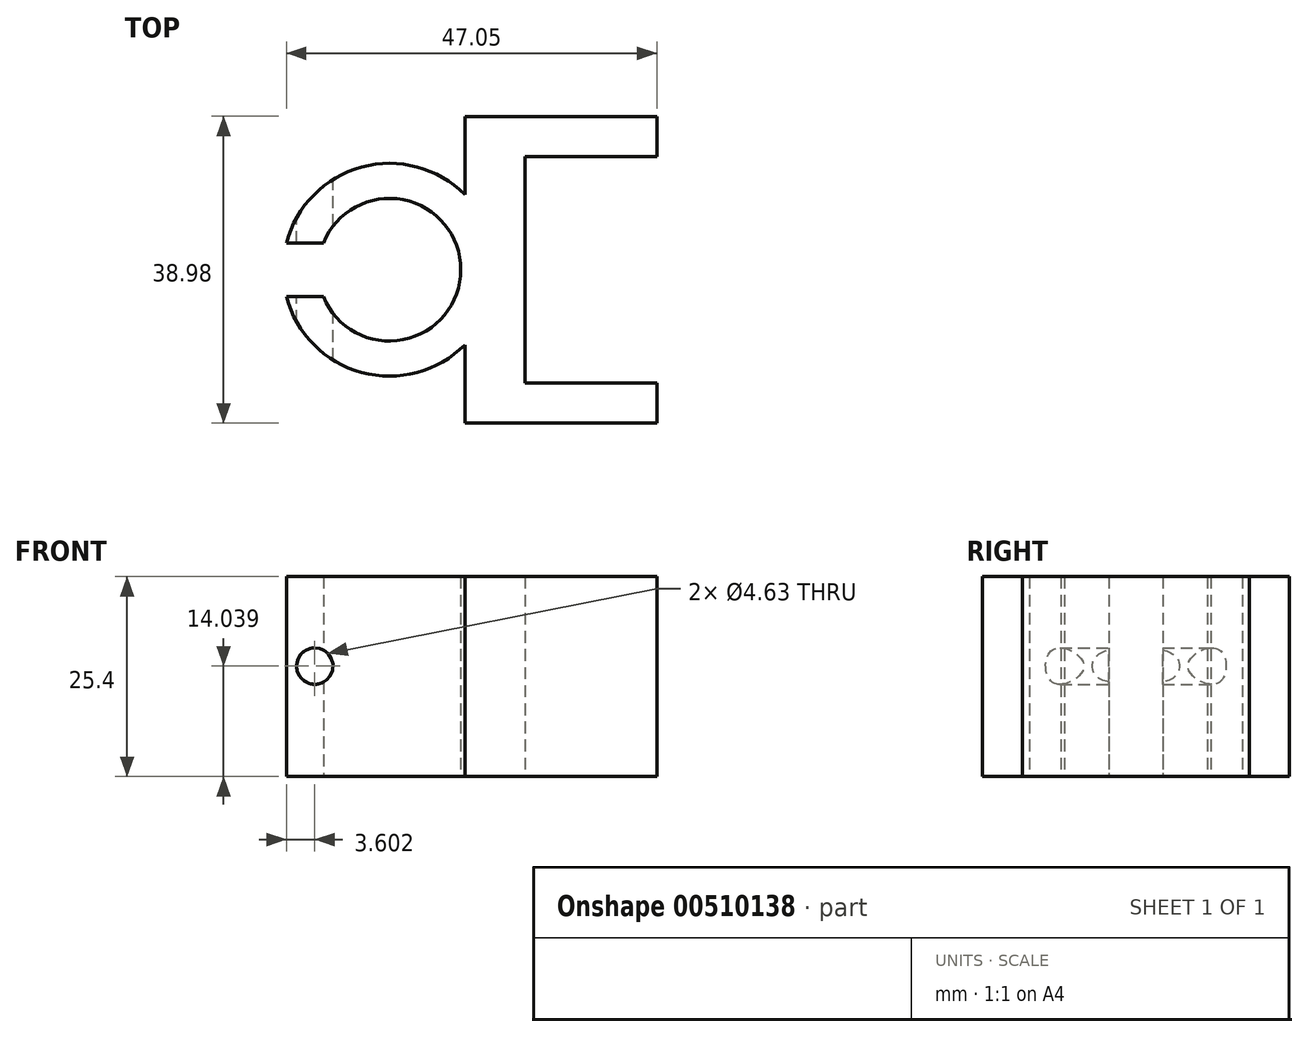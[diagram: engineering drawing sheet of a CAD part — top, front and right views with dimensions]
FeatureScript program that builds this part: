
annotation { "Feature Type Name" : "Feature", "Feature Type Description" : "" }
export const myFeature = defineFeature(function(context is Context, id is Id, definition is map)
    precondition{}
    {
        {
            var Q0;
            Q0=qCreatedBy(makeId("Top.planeOp"),FACE);
            var sketch = newSketch(context, id + "F0", { "sketchPlane" : qUnion([Q0])});
            skCircle(sketch, "E0", {"center": v(-28.96, 0) * mm, "radius": 9.06 * mm});
            skCircle(sketch, "E1", {"center": v(-28.96, 0) * mm, "radius": 13.52 * mm});
            skLineSegment(sketch, "E2.bottom", {"start": v(-19.38, -19.49) * mm, "end": v(-11.76, -19.49) * mm});
            skLineSegment(sketch, "E2.top", {"start": v(-19.38, 19.49) * mm, "end": v(-11.76, 19.49) * mm});
            skLineSegment(sketch, "E2.left", {"start": v(-19.38, -19.49) * mm, "end": v(-19.38, 19.49) * mm});
            skLineSegment(sketch, "E2.right", {"start": v(-11.76, -19.49) * mm, "end": v(-11.76, 19.49) * mm});
            skLineSegment(sketch, "E3.bottom", {"start": v(-11.76, 19.49) * mm, "end": v(5, 19.49) * mm});
            skLineSegment(sketch, "E3.top", {"start": v(-11.76, 14.4) * mm, "end": v(5, 14.4) * mm});
            skLineSegment(sketch, "E3.left", {"start": v(-11.76, 19.49) * mm, "end": v(-11.76, 14.4) * mm});
            skLineSegment(sketch, "E3.right", {"start": v(5, 19.49) * mm, "end": v(5, 14.4) * mm});
            skLineSegment(sketch, "E4.bottom", {"start": v(-11.76, -19.49) * mm, "end": v(5, -19.49) * mm});
            skLineSegment(sketch, "E4.top", {"start": v(-11.76, -14.4) * mm, "end": v(5, -14.4) * mm});
            skLineSegment(sketch, "E4.left", {"start": v(-11.76, -19.49) * mm, "end": v(-11.76, -14.4) * mm});
            skLineSegment(sketch, "E4.right", {"start": v(5, -19.49) * mm, "end": v(5, -14.4) * mm});
            skPoint(sketch, "E5.0", {"position": v(0, 0) * mm});
            skSolve(sketch);
        }
        {
            var Q0;
            Q0 = qSketchRegion(id + "F0", true);
            extrude(context, id + "F1", {"entities" : qUnion([Q0]), "depth" : 25.4 * mm});
        }
        {
            var Q0;
            Q0=makeQuery(id+"F1.opExtrude","CAP_FACE",FACE,{"disambiguationData":[OSD([sQuery(id+"F0.wireOp",EDGE,"E0"),sQuery(id+"F0.wireOp",EDGE,"E1"),sQuery(id+"F0.wireOp",EDGE,"E2.bottom"),sQuery(id+"F0.wireOp",EDGE,"E2.top"),sQuery(id+"F0.wireOp",EDGE,"E2.left"),sQuery(id+"F0.wireOp",EDGE,"E2.right"),sQuery(id+"F0.wireOp",EDGE,"E3.bottom"),sQuery(id+"F0.wireOp",EDGE,"E3.top"),sQuery(id+"F0.wireOp",EDGE,"E3.right"),sQuery(id+"F0.wireOp",EDGE,"E4.bottom"),sQuery(id+"F0.wireOp",EDGE,"E4.top"),sQuery(id+"F0.wireOp",EDGE,"E4.right")])],"isStart":false});
            var sketch = newSketch(context, id + "F2", { "sketchPlane" : qUnion([Q0])});
            skLineSegment(sketch, "E6.bottom", {"start": v(-31.35, 3.4) * mm, "end": v(-44.68, 3.4) * mm});
            skLineSegment(sketch, "E6.top", {"start": v(-31.35, -3.4) * mm, "end": v(-44.68, -3.4) * mm});
            skLineSegment(sketch, "E6.left", {"start": v(-31.35, 3.4) * mm, "end": v(-31.35, -3.4) * mm});
            skLineSegment(sketch, "E6.right", {"start": v(-44.68, 3.4) * mm, "end": v(-44.68, -3.4) * mm});
            skPoint(sketch, "E6.middle", {"position": v(-38.02, 0) * mm});
            skPoint(sketch, "E6.middle.positionSnap0", {"position": v(-42.48, 0) * mm});
            skPoint(sketch, "E6.centerSnap0", {"position": v(-42.48, 0) * mm});
            skSolve(sketch);
        }
        {
            var Q0;
            Q0 = qSketchRegion(id + "F2", true);
            extrude(context, id + "F3", {"entities" : qUnion([Q0]), "operationType" : NewBodyOperationType.REMOVE, "oppositeDirection" : true, "depth" : 25.4 * mm});
        }
        {
            var Q0;
            Q0=qCreatedBy(makeId("Front.planeOp"),FACE);
            var sketch = newSketch(context, id + "F4", { "sketchPlane" : qUnion([Q0])});
            skCircle(sketch, "E7", {"center": v(-38.44, 14.04) * mm, "radius": 2.31 * mm});
            skSolve(sketch);
        }
        {
            var Q0;
            Q0 = qSketchRegion(id + "F4", true);
            extrude(context, id + "F5", {"entities" : qUnion([Q0]), "operationType" : NewBodyOperationType.REMOVE, "depth" : 254 * mm, "symmetric" : true});
        }
    });
